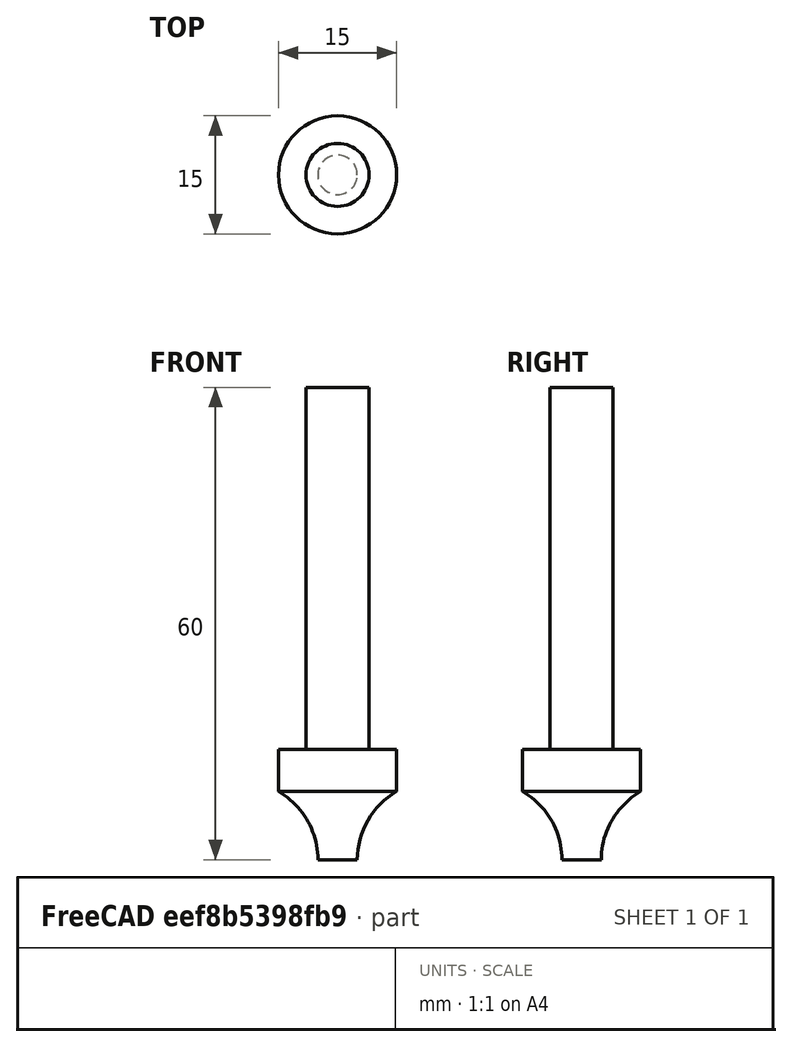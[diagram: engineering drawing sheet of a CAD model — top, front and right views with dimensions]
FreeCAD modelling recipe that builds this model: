
FCSTD DOCUMENT  (FreeCAD 1.1R43248 +2 (Git))
Label: radius
License: All rights reserved
LicenseURL: http://en.wikipedia.org/wiki/All_rights_reserved
objects: Sketcher::SketchObject×1, PartDesign::Revolution×1, App::FeaturePython×1, PartDesign::Body×1, App::Point×1
note: 6 computed .brp shape members not serialized (recipe doc carries the construction recipe); baked Part::Feature solids carry a one-line shape summary decoded from their .brp

FEATURE [Sketcher::SketchObject] Sketch
  ArcFitTolerance = 0
  AttachmentSupport = -> [XZ_Plane]
  ExternalTypes = [0]
  FullyConstrained = true
  MakeInternals = false
  MapMode = 5
  Placement = pos=(0,0,0) rot=(1,0,0;1.5708rad)
  expr: Constraints[10] = <<Attributes>>.ShankDiameter / 2
  expr: Constraints[11] = <<Attributes>>.TipDiameter / 2 + 1 um
  expr: Constraints[18] = <<Attributes>>.CuttingEdgeHeight
  expr: Constraints[19] = <<Attributes>>.CuttingRadius
  expr: Constraints[20] = <<Attributes>>.Diameter
  expr: Constraints[4] = <<Attributes>>.Length
  sketch-geometry (8):
    g0: LineSegment StartX=0 StartY=60 StartZ=0 EndX=0 EndY=0 EndZ=0
    g1: LineSegment StartX=0 StartY=0 StartZ=0 EndX=2.501 EndY=0 EndZ=0
    g2: LineSegment StartX=4 StartY=60 StartZ=0 EndX=0 EndY=60 EndZ=0
    g3: LineSegment StartX=4 StartY=14.01 StartZ=0 EndX=7.5 EndY=14 EndZ=0
    g4: LineSegment StartX=4 StartY=60 StartZ=0 EndX=4 EndY=14.01 EndZ=0
    g5: ArcOfCircle CenterX=12.501 CenterY=0 CenterZ=0 NormalX=0 NormalY=0 NormalZ=1 AngleXU=0 Radius=10 StartAngle=2.09451 EndAngle=3.14159
    g6: LineSegment StartX=7.5 StartY=14 StartZ=0 EndX=7.5 EndY=8.65968 EndZ=0
    g7: LineSegment [constr] StartX=-7.5 StartY=14 StartZ=0 EndX=7.5 EndY=14 EndZ=0
  constraints (23):
    c: Vertical(g0)
    c: Coincident(g0,g1)
    c: Horizontal(g1)
    c: Horizontal(g2)
    c: DistanceY(g1,g2) = 60
    c: Vertical(g4)
    c: Coincident(g2,g4)
    c: Coincident(g3,g4)
    c: Coincident(g0,g-1)
    c: Coincident(g0,g2)
    c: DistanceX(g-2,g2) = 4
    c: DistanceX(g-2,g1) = 2.501
    c: DistanceY(g3,g3) = 0.01
    c: PointOnObject(g5,g-1)
    c: Coincident(g6,g3)
    c: Vertical(g6)
    c: Coincident(g5,g1)
    c: Coincident(g5,g6)
    c: DistanceY(g1,g3) = 14
    c: Radius(g5) = 10
    c: DistanceX(g7,g7) = 15
    c: Symmetric(g7,g7,g0)
    c: Coincident(g7,g3)
FEATURE [PartDesign::Revolution] Revolution
  AllowMultiFace = false
  Angle = 360
  Angle2 = 60
  Axis = (0,2e-16,1)
  Base = (0,0,0)
  Placement = pos=(0,0,0) rot=(1,0,0;1.5708rad)
  Profile = -> Sketch
  ReferenceAxis = -> Sketch [V_Axis]
  Reversed = true
  Suppressed = false
  Type = 0
FEATURE [App::FeaturePython] PropertyBag  label="Attributes"  # WARN: FeaturePython — macro-defined, semantics opaque (R4)
  CustomPropertyGroups = 0
  CuttingEdgeHeight = 14
  CuttingRadius = 10
  Diameter = 15
  Flutes = 2
  Length = 60
  ShankDiameter = 8
  TipDiameter = 5
FEATURE [PartDesign::Body] Body  label="Radius"
  AllowCompound = false
  Group = -> [Sketch,Revolution,PropertyBag]
  Origin = -> Origin
  Tip = -> Revolution
FEATURE [App::Point] Origin001  label="Origin"
  Role = Origin
